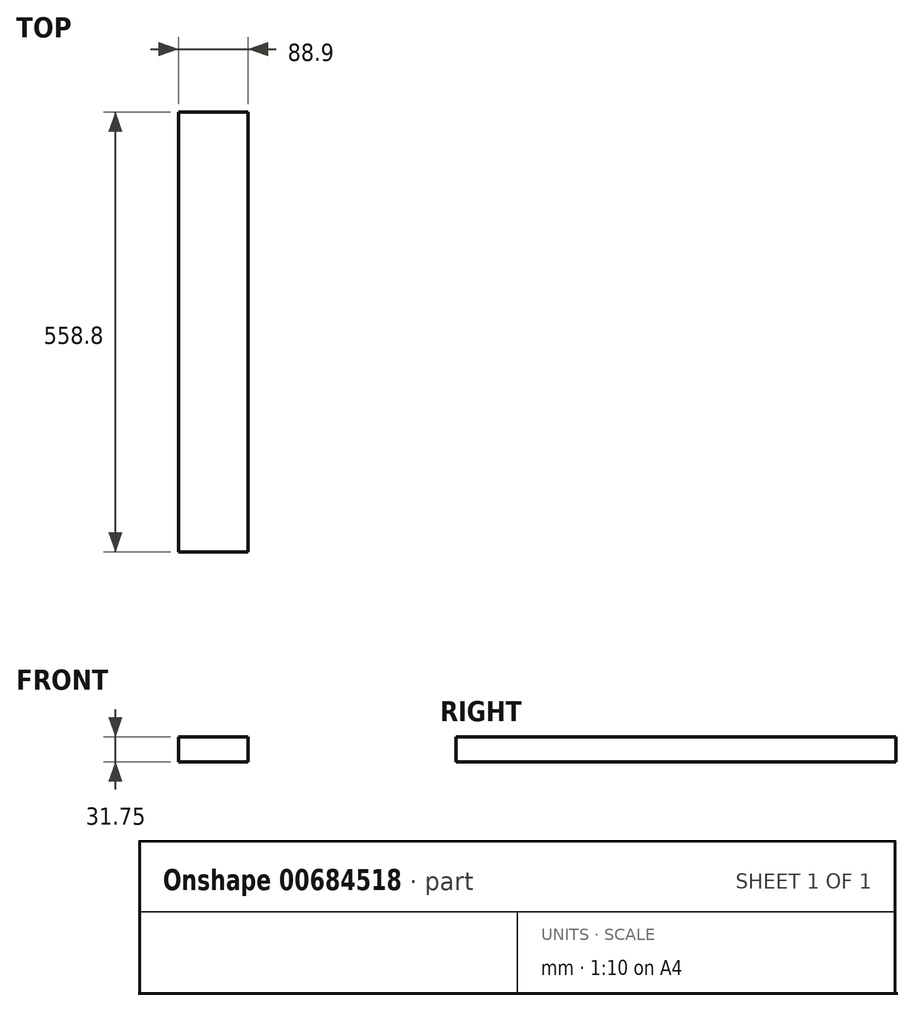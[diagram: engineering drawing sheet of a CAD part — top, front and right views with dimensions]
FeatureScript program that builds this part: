
annotation { "Feature Type Name" : "Feature", "Feature Type Description" : "" }
export const myFeature = defineFeature(function(context is Context, id is Id, definition is map)
    precondition{}
    {
        {
            var Q0;
            Q0=qCreatedBy(makeId("Top.planeOp"),FACE);
            var sketch = newSketch(context, id + "F0", { "sketchPlane" : qUnion([Q0])});
            skLineSegment(sketch, "E0.bottom", {"start": v(-85.4, 414.19) * mm, "end": v(3.5, 414.19) * mm});
            skLineSegment(sketch, "E0.top", {"start": v(-85.4, -144.61) * mm, "end": v(3.5, -144.61) * mm});
            skLineSegment(sketch, "E0.left", {"start": v(-85.4, 414.19) * mm, "end": v(-85.4, -144.61) * mm});
            skLineSegment(sketch, "E0.right", {"start": v(3.5, 414.19) * mm, "end": v(3.5, -144.61) * mm});
            skSolve(sketch);
        }
        {
            var Q0;
            Q0 = qSketchRegion(id + "F0", true);
            extrude(context, id + "F1", {"entities" : qUnion([Q0]), "depth" : 31.75 * mm, "offsetDistance" : 25.4 * mm});
        }
    });
